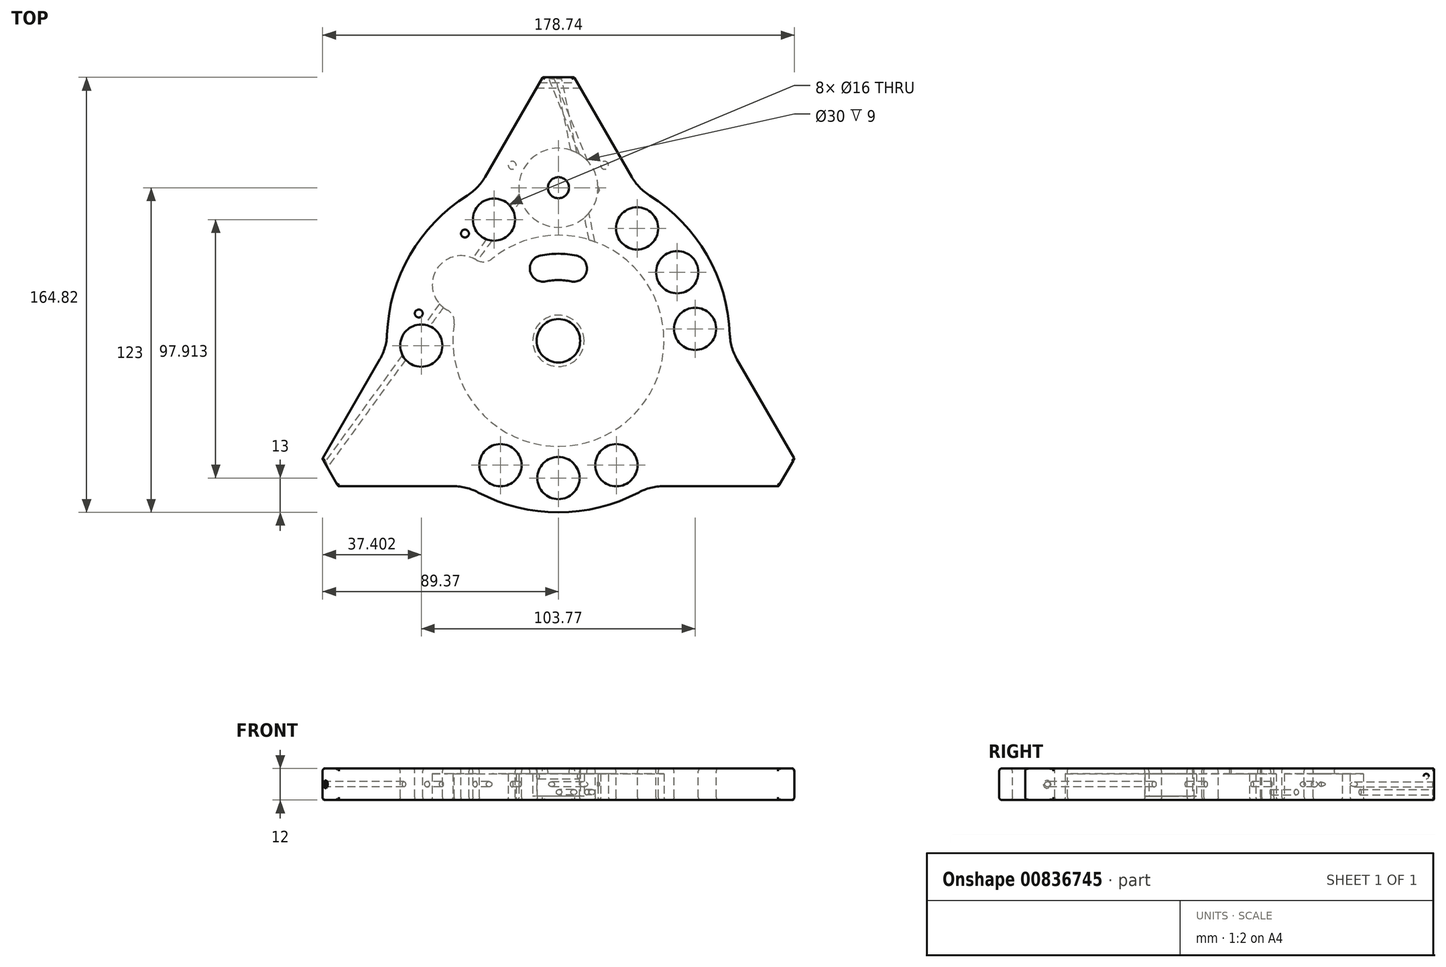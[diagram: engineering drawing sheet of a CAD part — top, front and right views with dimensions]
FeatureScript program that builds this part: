
annotation { "Feature Type Name" : "Feature", "Feature Type Description" : "" }
export const myFeature = defineFeature(function(context is Context, id is Id, definition is map)
    precondition{}
    {
        {
            var Q0;
            Q0=qCreatedBy(makeId("Top.planeOp"),FACE);
            var sketch = newSketch(context, id + "F0", { "sketchPlane" : qUnion([Q0])});
            skCircle(sketch, "E0", {"center": v(0, 0) * mm, "radius": 100 * mm, "construction": true});
            skCircle(sketch, "E1", {"center": v(0, 0) * mm, "radius": 65 * mm});
            skLineSegment(sketch, "E2", {"start": v(-6, 99.82) * mm, "end": v(-89.45, -44.71) * mm});
            skLineSegment(sketch, "E3", {"start": v(-89.45, -44.71) * mm, "end": v(-83.45, -55.1) * mm});
            skLineSegment(sketch, "E4", {"start": v(-83.45, -55.1) * mm, "end": v(83.45, -55.1) * mm});
            skLineSegment(sketch, "E5", {"start": v(83.45, -55.1) * mm, "end": v(89.45, -44.71) * mm});
            skLineSegment(sketch, "E6", {"start": v(89.45, -44.71) * mm, "end": v(6, 99.82) * mm});
            skLineSegment(sketch, "E7", {"start": v(6, 99.82) * mm, "end": v(-6, 99.82) * mm});
            skLineSegment(sketch, "E8", {"start": v(-86.6, -50) * mm, "end": v(0, 0) * mm, "construction": true});
            skLineSegment(sketch, "E9", {"start": v(0, 0) * mm, "end": v(86.45, -49.9) * mm, "construction": true});
            skSolve(sketch);
        }
        {
            var Q0;
            Q0=qSketchRegion(id+"F0",true);
            extrude(context, id + "F1", {"entities" : qUnion([Q0]), "depth" : 12 * mm, "offsetDistance" : 25 * mm});
        }
        {
            var Q0;
            Q0=qCreatedBy(makeId("Top.planeOp"),FACE);
            var sketch = newSketch(context, id + "F2", { "sketchPlane" : qUnion([Q0])});
            skCircle(sketch, "E10", {"center": v(0, 0) * mm, "radius": 8.25 * mm});
            skSolve(sketch);
        }
        {
            var Q0;
            Q0=qSketchRegion(id+"F2",true);
            extrude(context, id + "F3", {"entities" : qUnion([Q0]), "operationType" : NewBodyOperationType.REMOVE, "depth" : 100 * mm, "offsetDistance" : 25 * mm});
        }
        {
            var Q0;
            Q0=qCreatedBy(makeId("Top.planeOp"),FACE);
            var sketch = newSketch(context, id + "F4", { "sketchPlane" : qUnion([Q0])});
            skCircle(sketch, "E11", {"center": v(0, 58) * mm, "radius": 15 * mm});
            skCircle(sketch, "E12", {"center": v(-17.5, 66.5) * mm, "radius": 1.5 * mm});
            skCircle(sketch, "E13", {"center": v(17.5, 66.5) * mm, "radius": 1.5 * mm});
            skCircle(sketch, "E14", {"center": v(0, 58) * mm, "radius": 4 * mm});
            skSolve(sketch);
        }
        {
            var Q0;
            Q0=makeQuery(id+"F4.imprint","IMPRINT",FACE,{"disambiguationData":[TD([[makeQuery(id+"F4.imprint","IMPRINT",EDGE,{"derivedFrom":sQuery(id+"F4.wireOp",EDGE,"E14")}),1.0]])]});
            var Q1;
            Q1=makeQuery(id+"F4.imprint","IMPRINT",FACE,{"disambiguationData":[TD([[makeQuery(id+"F4.imprint","IMPRINT",EDGE,{"derivedFrom":sQuery(id+"F4.wireOp",EDGE,"E11")}),1.0]])]});
            var Q2;
            Q2=makeQuery(id+"F4.imprint","IMPRINT",FACE,{"disambiguationData":[TD([[makeQuery(id+"F4.imprint","IMPRINT",EDGE,{"derivedFrom":sQuery(id+"F4.wireOp",EDGE,"E13")}),1.0]])]});
            var Q3;
            Q3=makeQuery(id+"F4.imprint","IMPRINT",FACE,{"disambiguationData":[TD([[makeQuery(id+"F4.imprint","IMPRINT",EDGE,{"derivedFrom":sQuery(id+"F4.wireOp",EDGE,"E12")}),1.0]])]});
            extrude(context, id + "F5", {"entities" : qUnion([Q0, Q1, Q2, Q3]), "operationType" : NewBodyOperationType.REMOVE, "depth" : 10 * mm, "offsetDistance" : 25 * mm});
        }
        {
            var Q0;
            Q0=makeQuery(id+"F4.imprint","IMPRINT",FACE,{"disambiguationData":[TD([[makeQuery(id+"F4.imprint","IMPRINT",EDGE,{"derivedFrom":sQuery(id+"F4.wireOp",EDGE,"E14")}),1.0]])]});
            extrude(context, id + "F6", {"entities" : qUnion([Q0]), "operationType" : NewBodyOperationType.REMOVE, "depth" : 25 * mm, "offsetDistance" : 25 * mm});
        }
        {
            var Q0;
            Q0=qCreatedBy(makeId("Top.planeOp"),FACE);
            var sketch = newSketch(context, id + "F7", { "sketchPlane" : qUnion([Q0])});
            skCircle(sketch, "E15", {"center": v(0, 0) * mm, "radius": 40 * mm});
            skCircle(sketch, "E16", {"center": v(0, 0) * mm, "radius": 9.75 * mm});
            skSolve(sketch);
        }
        {
            var Q0;
            Q0=qSketchRegion(id+"F7",true);
            extrude(context, id + "F8", {"entities" : qUnion([Q0]), "operationType" : NewBodyOperationType.REMOVE, "depth" : 10 * mm, "offsetDistance" : 25 * mm});
        }
        {
            var Q0;
            Q0=qCreatedBy(makeId("Top.planeOp"),FACE);
            var sketch = newSketch(context, id + "F9", { "sketchPlane" : qUnion([Q0])});
            skCircle(sketch, "E17", {"center": v(-36.8, 21.25) * mm, "radius": 11 * mm});
            skLineSegment(sketch, "E18", {"start": v(-36.8, 21.25) * mm, "end": v(0, 0) * mm, "construction": true});
            skCircle(sketch, "E19", {"center": v(-36.8, 21.25) * mm, "radius": 5 * mm});
            skSolve(sketch);
        }
        {
            var Q0;
            Q0=makeQuery(id+"F9.imprint","IMPRINT",FACE,{"disambiguationData":[TD([[makeQuery(id+"F9.imprint","IMPRINT",EDGE,{"derivedFrom":sQuery(id+"F9.wireOp",EDGE,"E19")}),1.0]])]});
            var Q1;
            Q1=makeQuery(id+"F9.imprint","IMPRINT",FACE,{"disambiguationData":[TD([[makeQuery(id+"F9.imprint","IMPRINT",EDGE,{"derivedFrom":sQuery(id+"F9.wireOp",EDGE,"E17")}),1.0]])]});
            extrude(context, id + "F10", {"entities" : qUnion([Q0, Q1]), "operationType" : NewBodyOperationType.REMOVE, "depth" : 10 * mm, "offsetDistance" : 25 * mm});
        }
        {
            var Q0;
            Q0=qCreatedBy(makeId("Top.planeOp"),FACE);
            var sketch = newSketch(context, id + "F11", { "sketchPlane" : qUnion([Q0])});
            skLineSegment(sketch, "E20", {"start": v(0, 0) * mm, "end": v(-36.8, 21.25) * mm, "construction": true});
            skLineSegment(sketch, "E21", {"start": v(-35.42, 40.66) * mm, "end": v(-52.92, 10.34) * mm, "construction": true});
            skCircle(sketch, "E22", {"center": v(-35.42, 40.66) * mm, "radius": 1.5 * mm});
            skCircle(sketch, "E23", {"center": v(-52.92, 10.34) * mm, "radius": 1.5 * mm});
            skCircle(sketch, "E24", {"center": v(-35.42, 40.66) * mm, "radius": 4 * mm});
            skCircle(sketch, "E25", {"center": v(-52.92, 10.34) * mm, "radius": 4 * mm});
            skSolve(sketch);
        }
        {
            var Q0;
            Q0=makeQuery(id+"F11.imprint","IMPRINT",FACE,{"disambiguationData":[TD([[makeQuery(id+"F11.imprint","IMPRINT",EDGE,{"derivedFrom":sQuery(id+"F11.wireOp",EDGE,"E22")}),1.0]])]});
            var Q1;
            Q1=makeQuery(id+"F11.imprint","IMPRINT",FACE,{"disambiguationData":[TD([[makeQuery(id+"F11.imprint","IMPRINT",EDGE,{"derivedFrom":sQuery(id+"F11.wireOp",EDGE,"E23")}),1.0]])]});
            extrude(context, id + "F12", {"entities" : qUnion([Q0, Q1]), "operationType" : NewBodyOperationType.REMOVE, "endBound" : BoundingType.SYMMETRIC, "oppositeDirection" : true, "depth" : 100 * mm, "offsetDistance" : 25 * mm});
        }
        {
            var Q0;
            Q0=qCreatedBy(makeId("Top.planeOp"),FACE);
            cPlane(context, id + "F13", {"entities" : qUnion([Q0]), "cplaneType" : CPlaneType.OFFSET, "offset" : 3 * mm, "width" : 150 * mm, "height" : 150 * mm});
        }
        {
            var Q0;
            Q0=makeQuery(id+"F10.boolean.opBoolean","INTERSECT",EDGE,{"disambiguationData":[OD(1.0)],"derivedFrom":[makeQuery(id+"F8.boolean.opBoolean","COPY",FACE,{"derivedFrom":makeQuery(id+"F8.opExtrude","SWEPT_FACE",FACE,{"disambiguationData":[OSD([sQuery(id+"F7.wireOp",EDGE,"E15")])]})}),makeQuery(id+"F10.opExtrude","SWEPT_FACE",FACE,{"disambiguationData":[OSD([sQuery(id+"F9.wireOp",EDGE,"E17")])]})]});
            var Q1;
            Q1=makeQuery(id+"F10.boolean.opBoolean","INTERSECT",EDGE,{"disambiguationData":[OD(0.0)],"derivedFrom":[makeQuery(id+"F8.boolean.opBoolean","COPY",FACE,{"derivedFrom":makeQuery(id+"F8.opExtrude","SWEPT_FACE",FACE,{"disambiguationData":[OSD([sQuery(id+"F7.wireOp",EDGE,"E15")])]})}),makeQuery(id+"F10.opExtrude","SWEPT_FACE",FACE,{"disambiguationData":[OSD([sQuery(id+"F9.wireOp",EDGE,"E17")])]})]});
            fillet(context, id + "F14", {"entities" : qUnion([Q0, Q1]), "radius" : 5 * mm, "tangentPropagation" : true, "allowEdgeOverflow" : false});
        }
        {
            var Q0;
            Q0=qCreatedBy(id+"F13.planeOp",FACE);
            var sketch = newSketch(context, id + "F15", { "sketchPlane" : qUnion([Q0])});
            skCircle(sketch, "E26", {"center": v(0, 0) * mm, "radius": 20 * mm, "construction": true});
            skLineSegment(sketch, "E27", {"start": v(19.6, 3.98) * mm, "end": v(0, 100.5) * mm});
            skCircle(sketch, "E28", {"center": v(0, 0) * mm, "radius": 100.5 * mm, "construction": true});
            skLineSegment(sketch, "E29", {"start": v(19.6, 3.98) * mm, "end": v(20.58, 4.18) * mm});
            skLineSegment(sketch, "E30", {"start": v(20.58, 4.18) * mm, "end": v(0.98, 100.7) * mm});
            skLineSegment(sketch, "E31", {"start": v(0.98, 100.7) * mm, "end": v(0, 100.5) * mm});
            skSolve(sketch);
        }
        {
            var Q0;
            Q0=makeQuery(id+"F15.imprint","IMPRINT",FACE,{"disambiguationData":[TD([[makeQuery(id+"F15.imprint","IMPRINT",EDGE,{"derivedFrom":sQuery(id+"F15.wireOp",EDGE,"E27")}),-1.0]])]});
            var Q1;
            Q1=sQuery(id+"F15.wireOp",EDGE,"E27");
            revolve(context, id + "F16", {"operationType" : NewBodyOperationType.REMOVE, "surfaceOperationType" : NewSurfaceOperationType.NEW, "entities" : qUnion([Q0]), "axis" : qUnion([Q1]), "revolveType" : RevolveType.FULL, "oppositeDirection" : true});
        }
        {
            var Q0;
            Q0=qCreatedBy(makeId("Top.planeOp"),FACE);
            cPlane(context, id + "F17", {"entities" : qUnion([Q0]), "cplaneType" : CPlaneType.OFFSET, "offset" : 6 * mm, "width" : 150 * mm, "height" : 150 * mm});
        }
        {
            var Q0;
            Q0=qCreatedBy(id+"F17.planeOp",FACE);
            var sketch = newSketch(context, id + "F18", { "sketchPlane" : qUnion([Q0])});
            skCircle(sketch, "E32", {"center": v(0, 0) * mm, "radius": 58 * mm, "construction": true});
            skCircle(sketch, "E33", {"center": v(0, 0) * mm, "radius": 100.5 * mm, "construction": true});
            skLineSegment(sketch, "E34", {"start": v(15, 56.03) * mm, "end": v(-3, 100.46) * mm});
            skLineSegment(sketch, "E35", {"start": v(-3, 100.46) * mm, "end": v(-4, 100.42) * mm});
            skLineSegment(sketch, "E36", {"start": v(-4, 100.42) * mm, "end": v(13.87, 56.32) * mm});
            skLineSegment(sketch, "E37", {"start": v(13.87, 56.32) * mm, "end": v(15, 56.03) * mm});
            skLineSegment(sketch, "E38", {"start": v(-13, 56.52) * mm, "end": v(-88.5, -47.63) * mm});
            skLineSegment(sketch, "E39", {"start": v(-88.5, -47.63) * mm, "end": v(-89.02, -46.65) * mm});
            skLineSegment(sketch, "E40", {"start": v(-89.02, -46.65) * mm, "end": v(-14.5, 56.16) * mm});
            skLineSegment(sketch, "E41", {"start": v(-13, 56.52) * mm, "end": v(-14.5, 56.16) * mm});
            skLineSegment(sketch, "E42", {"start": v(0, 0) * mm, "end": v(-87.04, -50.25) * mm, "construction": true});
            skSolve(sketch);
        }
        {
            var Q0;
            Q0=makeQuery(id+"F18.imprint","IMPRINT",FACE,{"disambiguationData":[TD([[makeQuery(id+"F18.imprint","IMPRINT",EDGE,{"derivedFrom":sQuery(id+"F18.wireOp",EDGE,"E34")}),1.0]])]});
            var Q1;
            Q1=sQuery(id+"F18.wireOp",EDGE,"E34");
            revolve(context, id + "F19", {"operationType" : NewBodyOperationType.REMOVE, "surfaceOperationType" : NewSurfaceOperationType.NEW, "entities" : qUnion([Q0]), "axis" : qUnion([Q1]), "revolveType" : RevolveType.FULL, "oppositeDirection" : true});
        }
        {
            var Q0;
            Q0=makeQuery(id+"F18.imprint","IMPRINT",FACE,{"disambiguationData":[TD([[makeQuery(id+"F18.imprint","IMPRINT",EDGE,{"derivedFrom":sQuery(id+"F18.wireOp",EDGE,"E38")}),-1.0]])]});
            var Q1;
            Q1=sQuery(id+"F18.wireOp",EDGE,"E38");
            revolve(context, id + "F20", {"operationType" : NewBodyOperationType.REMOVE, "surfaceOperationType" : NewSurfaceOperationType.NEW, "entities" : qUnion([Q0]), "axis" : qUnion([Q1]), "revolveType" : RevolveType.FULL, "oppositeDirection" : true});
        }
        {
            var Q0;
            Q0=qCreatedBy(makeId("Top.planeOp"),FACE);
            var sketch = newSketch(context, id + "F21", { "sketchPlane" : qUnion([Q0])});
            skCircle(sketch, "E43", {"center": v(0, 0) * mm, "radius": 10 * mm});
            skSolve(sketch);
        }
        {
            var Q0;
            Q0=makeQuery(id+"F21.imprint","IMPRINT",FACE,{"disambiguationData":[TD([[makeQuery(id+"F21.imprint","IMPRINT",EDGE,{"derivedFrom":sQuery(id+"F21.wireOp",EDGE,"E43")}),1.0]])]});
            extrude(context, id + "F22", {"entities" : qUnion([Q0]), "operationType" : NewBodyOperationType.REMOVE, "depth" : 1.5 * mm, "offsetDistance" : 25 * mm});
        }
        {
            var Q0;
            Q0=qCreatedBy(makeId("Right.planeOp"),FACE);
            var sketch = newSketch(context, id + "F23", { "sketchPlane" : qUnion([Q0])});
            skCircle(sketch, "E44", {"center": v(96.82, 9) * mm, "radius": 1 * mm});
            skSolve(sketch);
        }
        {
            var Q0;
            Q0=qSketchRegion(id+"F23",true);
            extrude(context, id + "F24", {"entities" : qUnion([Q0]), "operationType" : NewBodyOperationType.REMOVE, "endBound" : BoundingType.SYMMETRIC, "oppositeDirection" : true, "depth" : 25 * mm, "offsetDistance" : 25 * mm});
        }
        {
            var Q0;
            {var subQ0=sQuery(id+"F0.wireOp",EDGE,"E2");var subQ1=sQuery(id+"F0.wireOp",EDGE,"E1");Q0=makeQuery(id+"F1.opExtrude","SWEPT_EDGE",EDGE,{"disambiguationData":[OSD([subQ1,subQ0]),TDD([makeQuery(id+"F0.imprint","INTERSECT",VERTEX,{"disambiguationData":[OD(0.0)],"derivedFrom":[subQ1,subQ0]})])]});}
            var Q1;
            {var subQ0=sQuery(id+"F0.wireOp",EDGE,"E2");var subQ1=sQuery(id+"F0.wireOp",EDGE,"E1");Q1=makeQuery(id+"F1.opExtrude","SWEPT_EDGE",EDGE,{"disambiguationData":[OSD([subQ1,subQ0]),TDD([makeQuery(id+"F0.imprint","INTERSECT",VERTEX,{"disambiguationData":[OD(1.0)],"derivedFrom":[subQ1,subQ0]})])]});}
            var Q2;
            {var subQ0=sQuery(id+"F0.wireOp",EDGE,"E4");var subQ1=sQuery(id+"F0.wireOp",EDGE,"E1");Q2=makeQuery(id+"F1.opExtrude","SWEPT_EDGE",EDGE,{"disambiguationData":[OSD([subQ1,subQ0]),TDD([makeQuery(id+"F0.imprint","INTERSECT",VERTEX,{"disambiguationData":[OD(0.0)],"derivedFrom":[subQ1,subQ0]})])]});}
            var Q3;
            {var subQ0=sQuery(id+"F0.wireOp",EDGE,"E4");var subQ1=sQuery(id+"F0.wireOp",EDGE,"E1");Q3=makeQuery(id+"F1.opExtrude","SWEPT_EDGE",EDGE,{"disambiguationData":[OSD([subQ1,subQ0]),TDD([makeQuery(id+"F0.imprint","INTERSECT",VERTEX,{"disambiguationData":[OD(1.0)],"derivedFrom":[subQ1,subQ0]})])]});}
            var Q4;
            {var subQ0=sQuery(id+"F0.wireOp",EDGE,"E6");var subQ1=sQuery(id+"F0.wireOp",EDGE,"E1");Q4=makeQuery(id+"F1.opExtrude","SWEPT_EDGE",EDGE,{"disambiguationData":[OSD([subQ1,subQ0]),TDD([makeQuery(id+"F0.imprint","INTERSECT",VERTEX,{"disambiguationData":[OD(1.0)],"derivedFrom":[subQ1,subQ0]})])]});}
            var Q5;
            {var subQ0=sQuery(id+"F0.wireOp",EDGE,"E6");var subQ1=sQuery(id+"F0.wireOp",EDGE,"E1");Q5=makeQuery(id+"F1.opExtrude","SWEPT_EDGE",EDGE,{"disambiguationData":[OSD([subQ1,subQ0]),TDD([makeQuery(id+"F0.imprint","INTERSECT",VERTEX,{"disambiguationData":[OD(0.0)],"derivedFrom":[subQ1,subQ0]})])]});}
            fillet(context, id + "F25", {"entities" : qUnion([Q0, Q1, Q2, Q3, Q4, Q5]), "radius" : 20 * mm, "tangentPropagation" : true, "allowEdgeOverflow" : false});
        }
        {
            var Q0;
            Q0=makeQuery(id+"F1.opExtrude","SWEPT_FACE",FACE,{"disambiguationData":[OSD([sQuery(id+"F0.wireOp",EDGE,"E7")])]});
            var Q1;
            Q1=makeQuery(id+"F1.opExtrude","SWEPT_FACE",FACE,{"disambiguationData":[OSD([sQuery(id+"F0.wireOp",EDGE,"E3")])]});
            var Q2;
            Q2=makeQuery(id+"F1.opExtrude","SWEPT_FACE",FACE,{"disambiguationData":[OSD([sQuery(id+"F0.wireOp",EDGE,"E5")])]});
            fillet(context, id + "F26", {"entities" : qUnion([Q0, Q1, Q2]), "radius" : 0.5 * mm, "tangentPropagation" : true, "allowEdgeOverflow" : false});
        }
        {
            var Q0;
            Q0=qCreatedBy(makeId("Top.planeOp"),FACE);
            var sketch = newSketch(context, id + "F27", { "sketchPlane" : qUnion([Q0])});
            skCircle(sketch, "E45", {"center": v(0, 0) * mm, "radius": 52 * mm, "construction": true});
            skCircle(sketch, "E46", {"center": v(29.83, 42.6) * mm, "radius": 8 * mm});
            skCircle(sketch, "E47", {"center": v(51.8, 4.53) * mm, "radius": 8 * mm});
            skCircle(sketch, "E48", {"center": v(21.98, -47.13) * mm, "radius": 8 * mm});
            skCircle(sketch, "E49", {"center": v(-21.98, -47.13) * mm, "radius": 8 * mm});
            skLineSegment(sketch, "E50", {"start": v(-21.98, -47.13) * mm, "end": v(0, 0) * mm, "construction": true});
            skLineSegment(sketch, "E51", {"start": v(21.98, -47.13) * mm, "end": v(0, 0) * mm, "construction": true});
            skLineSegment(sketch, "E52", {"start": v(51.8, 4.53) * mm, "end": v(0, 0) * mm, "construction": true});
            skLineSegment(sketch, "E53", {"start": v(29.83, 42.6) * mm, "end": v(0, 0) * mm, "construction": true});
            skCircle(sketch, "E54", {"center": v(0, -52) * mm, "radius": 8 * mm});
            skCircle(sketch, "E55", {"center": v(45.03, 26) * mm, "radius": 8 * mm});
            skLineSegment(sketch, "E56", {"start": v(45.03, 26) * mm, "end": v(0, 0) * mm, "construction": true});
            skCircle(sketch, "E57", {"center": v(-24.41, 45.91) * mm, "radius": 8 * mm});
            skCircle(sketch, "E58", {"center": v(-51.97, -1.81) * mm, "radius": 8 * mm});
            skLineSegment(sketch, "E59", {"start": v(0, 0) * mm, "end": v(-51.97, -1.81) * mm, "construction": true});
            skLineSegment(sketch, "E60", {"start": v(-24.41, 45.91) * mm, "end": v(0, 0) * mm, "construction": true});
            skSolve(sketch);
        }
        {
            var Q0;
            Q0=qSketchRegion(id+"F27",true);
            extrude(context, id + "F28", {"entities" : qUnion([Q0]), "operationType" : NewBodyOperationType.REMOVE, "endBound" : BoundingType.SYMMETRIC, "oppositeDirection" : true, "depth" : 100 * mm, "offsetDistance" : 25 * mm});
        }
        {
            var Q0;
            Q0=qCreatedBy(makeId("Top.planeOp"),FACE);
            var sketch = newSketch(context, id + "F29", { "sketchPlane" : qUnion([Q0])});
            skCircle(sketch, "E61", {"center": v(0, 0) * mm, "radius": 28 * mm, "construction": true});
            skCircle(sketch, "E62", {"center": v(5.82, 27.39) * mm, "radius": 5 * mm});
            skCircle(sketch, "E63", {"center": v(-5.82, 27.39) * mm, "radius": 5 * mm});
            skCircle(sketch, "E64", {"center": v(0, 0) * mm, "radius": 23 * mm});
            skCircle(sketch, "E65", {"center": v(0, 0) * mm, "radius": 33 * mm});
            skLineSegment(sketch, "E66", {"start": v(5.82, 27.39) * mm, "end": v(0, 0) * mm, "construction": true});
            skLineSegment(sketch, "E67", {"start": v(-5.82, 27.39) * mm, "end": v(0, 0) * mm, "construction": true});
            skSolve(sketch);
        }
        {
            var Q0;
            {var subQ0=sQuery(id+"F29.wireOp",EDGE,"E65");var subQ1=sQuery(id+"F29.wireOp",EDGE,"E62");var subQ2=makeQuery(id+"F29.imprint","INTERSECT",VERTEX,{"derivedFrom":[subQ1,subQ0]});Q0=makeQuery(id+"F29.imprint","IMPRINT",FACE,{"disambiguationData":[TD([[makeQuery(id+"F29.imprint","IMPRINT",EDGE,{"disambiguationData":[TD([[subQ2,-1.0]])],"derivedFrom":subQ1}),-1.0]])]});}
            var Q1;
            {var subQ0=sQuery(id+"F29.wireOp",EDGE,"E62");var subQ1=makeQuery(id+"F29.imprint","INTERSECT",VERTEX,{"derivedFrom":[subQ0,sQuery(id+"F29.wireOp",EDGE,"E65")]});Q1=makeQuery(id+"F29.imprint","IMPRINT",FACE,{"disambiguationData":[TD([[makeQuery(id+"F29.imprint","IMPRINT",EDGE,{"disambiguationData":[TD([[subQ1,-1.0]])],"derivedFrom":subQ0}),1.0]])]});}
            var Q2;
            {var subQ0=sQuery(id+"F29.wireOp",EDGE,"E63");var subQ1=makeQuery(id+"F29.imprint","INTERSECT",VERTEX,{"derivedFrom":[subQ0,sQuery(id+"F29.wireOp",EDGE,"E65")]});Q2=makeQuery(id+"F29.imprint","IMPRINT",FACE,{"disambiguationData":[TD([[makeQuery(id+"F29.imprint","IMPRINT",EDGE,{"disambiguationData":[TD([[subQ1,-1.0]])],"derivedFrom":subQ0}),1.0]])]});}
            extrude(context, id + "F30", {"entities" : qUnion([Q0, Q1, Q2]), "operationType" : NewBodyOperationType.REMOVE, "endBound" : BoundingType.SYMMETRIC, "oppositeDirection" : true, "depth" : 100 * mm, "offsetDistance" : 25 * mm});
        }
        {
            var Q0;
            Q0=makeQuery(id+"F1.opExtrude","CAP_FACE",FACE,{"disambiguationData":[OSD([sQuery(id+"F0.wireOp",EDGE,"E1"),sQuery(id+"F0.wireOp",EDGE,"E2"),sQuery(id+"F0.wireOp",EDGE,"E3"),sQuery(id+"F0.wireOp",EDGE,"E4"),sQuery(id+"F0.wireOp",EDGE,"E5"),sQuery(id+"F0.wireOp",EDGE,"E6"),sQuery(id+"F0.wireOp",EDGE,"E7")])],"isStart":false});
            var Q1;
            {var subQ0=sQuery(id+"F0.wireOp",EDGE,"E5");var subQ1=sQuery(id+"F0.wireOp",EDGE,"E4");var subQ2=sQuery(id+"F0.wireOp",EDGE,"E1");var subQ4=sQuery(id+"F0.wireOp",EDGE,"E3");var subQ7=sQuery(id+"F0.wireOp",EDGE,"E2");var subQ9=sQuery(id+"F0.wireOp",EDGE,"E6");var subQ13=sQuery(id+"F0.wireOp",EDGE,"E7");Q1=makeQuery(id+"F8.boolean.opBoolean","SPLIT",FACE,{"disambiguationData":[TD([makeQuery(id+"F1.opExtrude","SWEPT_FACE",FACE,{"disambiguationData":[OSD([subQ4])]})])],"derivedFrom":makeQuery(id+"F1.opExtrude","CAP_FACE",FACE,{"disambiguationData":[OSD([subQ2,subQ7,subQ4,subQ1,subQ0,subQ9,subQ13])],"isStart":true})});}
            fillet(context, id + "F31", {"entities" : qUnion([Q0, Q1]), "radius" : 1 * mm, "tangentPropagation" : true, "allowEdgeOverflow" : false});
        }
    });
